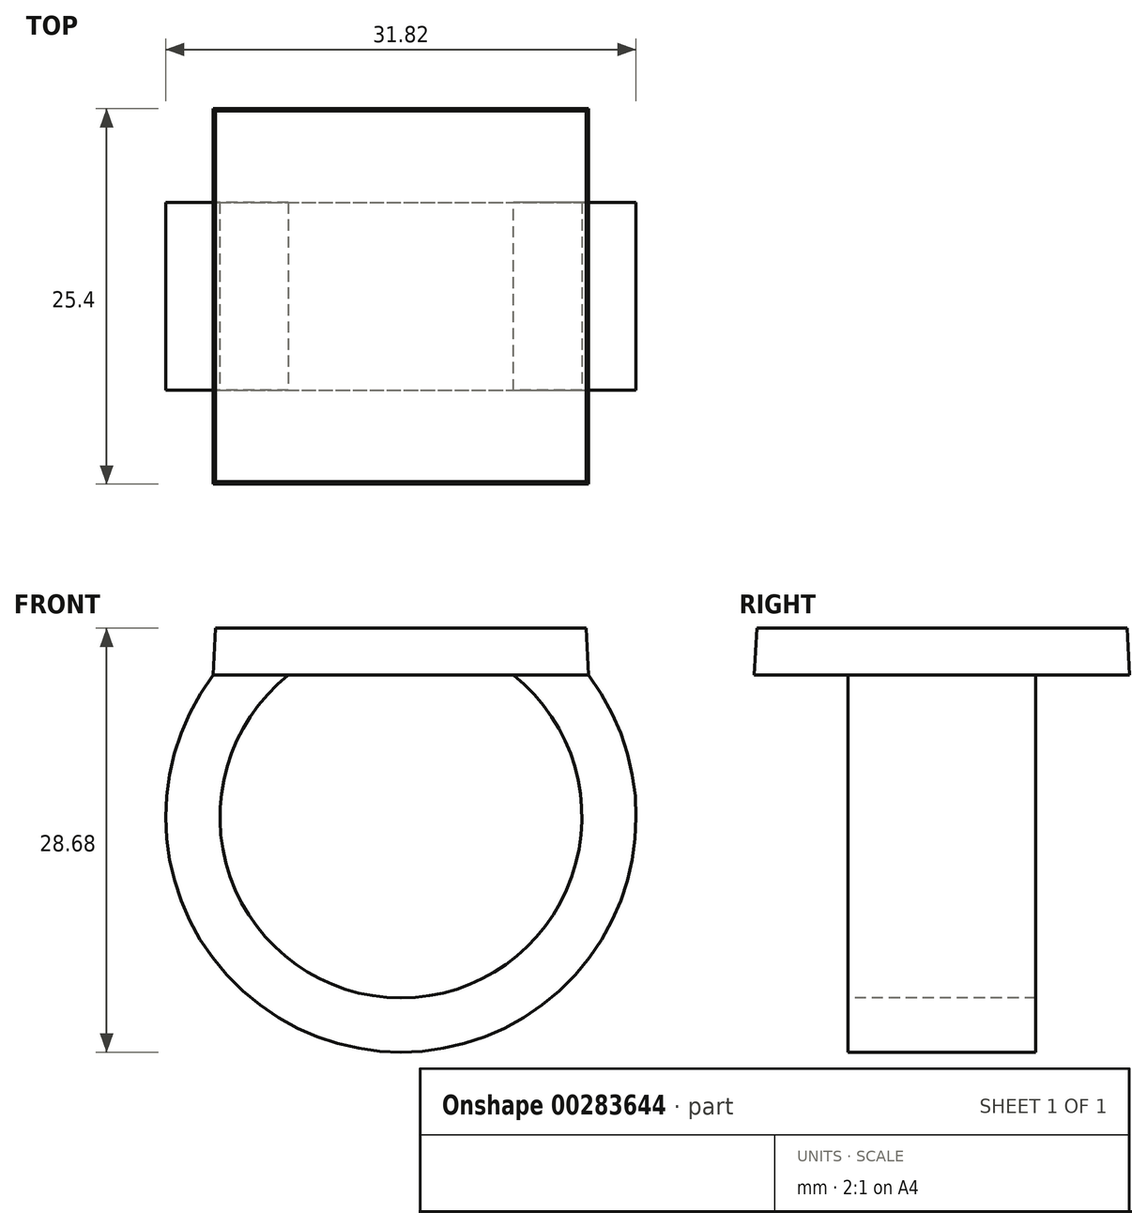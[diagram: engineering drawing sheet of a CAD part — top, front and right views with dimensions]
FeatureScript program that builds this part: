
annotation { "Feature Type Name" : "Feature", "Feature Type Description" : "" }
export const myFeature = defineFeature(function(context is Context, id is Id, definition is map)
    precondition{}
    {
        {
            var Q0;
            Q0=qCreatedBy(makeId("Top.planeOp"),FACE);
            var sketch = newSketch(context, id + "F0", { "sketchPlane" : qUnion([Q0])});
            skLineSegment(sketch, "E0.bottom", {"start": v(12.7, -12.7) * mm, "end": v(-12.7, -12.7) * mm});
            skLineSegment(sketch, "E0.top", {"start": v(12.7, 12.7) * mm, "end": v(-12.7, 12.7) * mm});
            skLineSegment(sketch, "E0.left", {"start": v(12.7, -12.7) * mm, "end": v(12.7, 12.7) * mm});
            skLineSegment(sketch, "E0.right", {"start": v(-12.7, -12.7) * mm, "end": v(-12.7, 12.7) * mm});
            skPoint(sketch, "E0.middle", {"position": v(0, 0) * mm});
            skSolve(sketch);
        }
        {
            var Q0;
            Q0 = qSketchRegion(id + "F0", true);
            extrude(context, id + "F1", {"entities" : qUnion([Q0]), "depth" : 3.17 * mm, "hasDraft" : true, "draftAngle" : 3 * degree, "draftPullDirection" : true});
        }
        {
            var Q0;
            Q0=qCreatedBy(makeId("Front.planeOp"),FACE);
            var sketch = newSketch(context, id + "F2", { "sketchPlane" : qUnion([Q0])});
            skArc(sketch, "E1", {"start": v(-10.16, 0) * mm, "mid": v(0, -23.56) * mm, "end": v(10.16, 0) * mm});
            skSolve(sketch);
        }
        {
            var Q0;
            Q0=makeQuery(id+"F1.opExtrude","CAP_FACE",FACE,{"disambiguationData":[OSD([sQuery(id+"F0.wireOp",EDGE,"E0.bottom"),sQuery(id+"F0.wireOp",EDGE,"E0.top"),sQuery(id+"F0.wireOp",EDGE,"E0.left"),sQuery(id+"F0.wireOp",EDGE,"E0.right")])],"isStart":true});
            var sketch = newSketch(context, id + "F3", { "sketchPlane" : qUnion([Q0])});
            skLineSegment(sketch, "E2.bottom", {"start": v(-7.62, -6.35) * mm, "end": v(-12.7, -6.35) * mm});
            skLineSegment(sketch, "E2.top", {"start": v(-7.62, 6.35) * mm, "end": v(-12.7, 6.35) * mm});
            skLineSegment(sketch, "E2.left", {"start": v(-7.62, -6.35) * mm, "end": v(-7.62, 6.35) * mm});
            skLineSegment(sketch, "E2.right", {"start": v(-12.7, -6.35) * mm, "end": v(-12.7, 6.35) * mm});
            skPoint(sketch, "E2.middle", {"position": v(-10.16, 0) * mm});
            skSolve(sketch);
        }
        {
            var Q0;
            Q0 = qSketchRegion(id + "F3", true);
            var Q1;
            Q1 = qConstructionFilter(qBodyType(qCreatedBy(id + "F2" ,EDGE), BodyType.WIRE), ConstructionObject.NO);
            sweep(context, id + "F4", {"operationType" : NewBodyOperationType.ADD, "profiles" : qUnion([Q0]), "path" : qUnion([Q1])});
        }
        {
            var Q0;
            Q0=qCreatedBy(makeId("Front.planeOp"),FACE);
            var sketch = newSketch(context, id + "F5", { "sketchPlane" : qUnion([Q0])});
            skLineSegment(sketch, "E3.0", {"start": v(10.16, 0) * mm, "end": v(7.62, 0) * mm});
            skLineSegment(sketch, "E4.0", {"start": v(10.01, -2.54) * mm, "end": v(10.16, 0) * mm});
            skLineSegment(sketch, "E5.0.1", {"start": v(10.16, 0) * mm, "end": v(10.01, -2.54) * mm});
            skArc(sketch, "E5.0.2", {"start": v(7.62, 0) * mm, "mid": v(8.9, -1.18) * mm, "end": v(10.01, -2.54) * mm});
            skArc(sketch, "E5.0.4", {"start": v(-12.7, 0) * mm, "mid": v(0, -25.5) * mm, "end": v(12.7, 0) * mm});
            skPoint(sketch, "E6.trimOffspring.end.orphan", {"position": v(-12.7, 0) * mm});
            skPoint(sketch, "E7.0.start.orphan", {"position": v(-7.62, 0) * mm});
            skPoint(sketch, "E8.orphan", {"position": v(12.7, 0) * mm});
            skSolve(sketch);
        }
        {
            var Q0;
            Q0 = qSketchRegion(id + "F5", true);
            var Q1;
            Q1=makeQuery(id+"F4.opSweep","SWEPT_FACE",FACE,{"disambiguationData":[OSD([sQuery(id+"F2.wireOp",EDGE,"E1"),sQuery(id+"F3.wireOp",EDGE,"E2.top")])]});
            var Q2;
            Q2=makeQuery(id+"F4.opSweep","SWEPT_FACE",FACE,{"disambiguationData":[OSD([sQuery(id+"F2.wireOp",EDGE,"E1"),sQuery(id+"F3.wireOp",EDGE,"E2.bottom")])]});
            extrude(context, id + "F6", {"entities" : qUnion([Q0]), "operationType" : NewBodyOperationType.ADD, "endBound" : BoundingType.UP_TO_SURFACE, "endBoundEntityFace" : qUnion([Q1]), "depth" : 25.4 * mm, "hasSecondDirection" : true, "secondDirectionBound" : SecondDirectionBoundingType.UP_TO_SURFACE, "secondDirectionOppositeDirection" : true, "secondDirectionBoundEntityFace" : qUnion([Q2]), "secondDirectionDepth" : 25.4 * mm});
        }
    });
